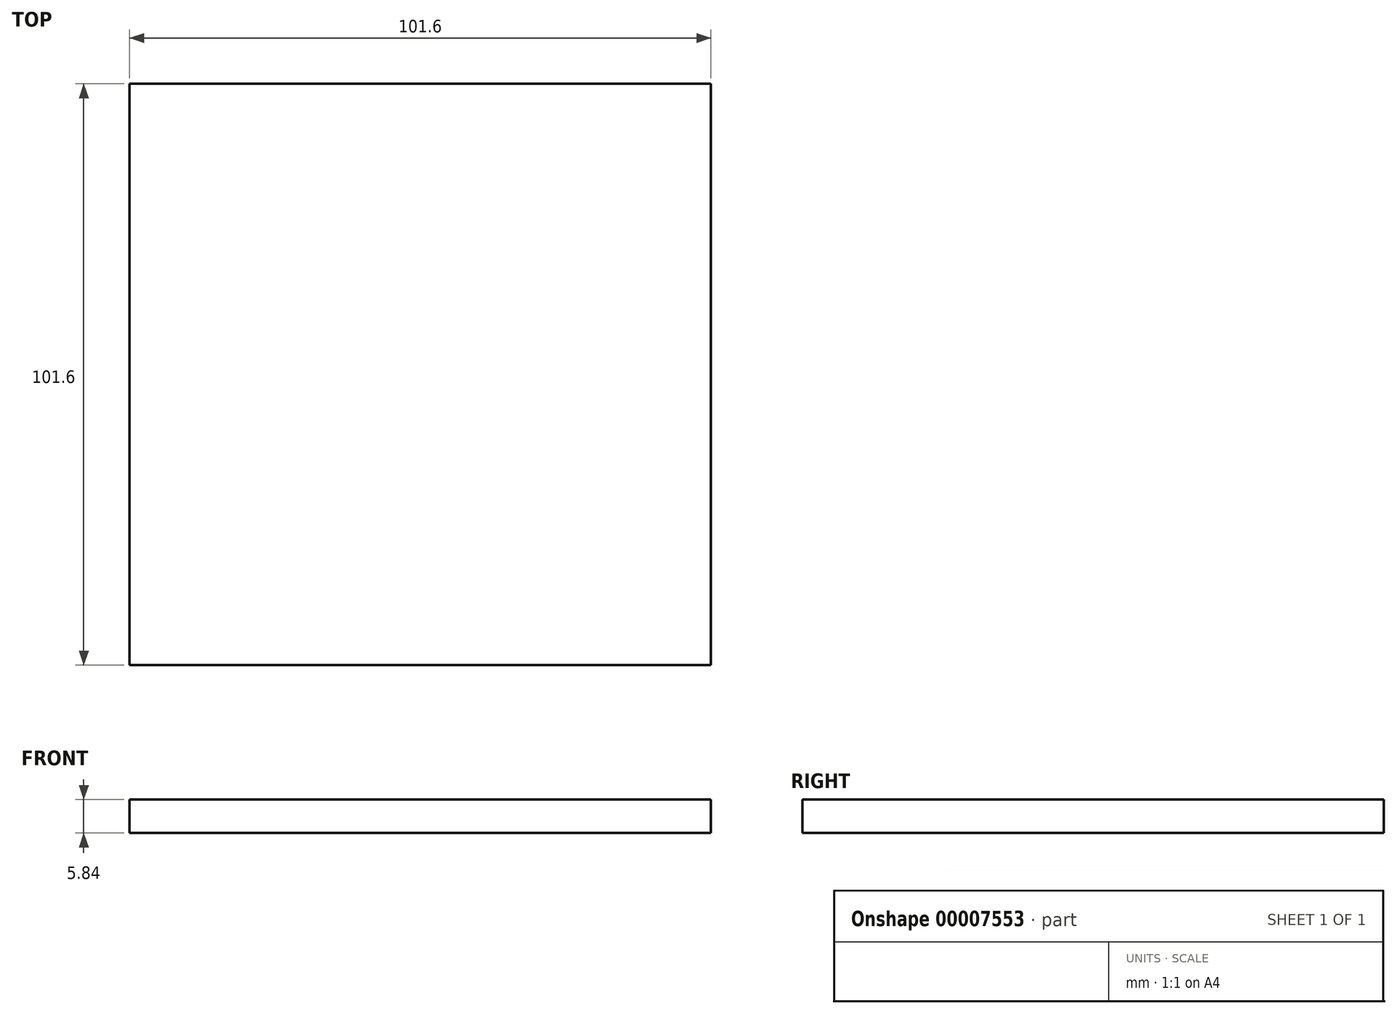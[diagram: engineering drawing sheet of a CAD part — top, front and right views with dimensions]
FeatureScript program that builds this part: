
annotation { "Feature Type Name" : "Feature", "Feature Type Description" : "" }
export const myFeature = defineFeature(function(context is Context, id is Id, definition is map)
    precondition{}
    {
        {
            var Q0;
            Q0=qCreatedBy(makeId("Top.planeOp"),FACE);
            var sketch = newSketch(context, id + "F0", { "sketchPlane" : qUnion([Q0])});
            skLineSegment(sketch, "E0.bottom", {"start": v(0, 0) * mm, "end": v(101.6, 0) * mm});
            skLineSegment(sketch, "E0.top", {"start": v(0, 101.6) * mm, "end": v(101.6, 101.6) * mm});
            skLineSegment(sketch, "E0.left", {"start": v(0, 0) * mm, "end": v(0, 101.6) * mm});
            skLineSegment(sketch, "E0.right", {"start": v(101.6, 0) * mm, "end": v(101.6, 101.6) * mm});
            skSolve(sketch);
        }
        {
            var Q0;
            Q0 = qSketchRegion(id + "F0", true);
            extrude(context, id + "F1", {"entities" : qUnion([Q0]), "depth" : 5.84 * mm});
        }
    });
